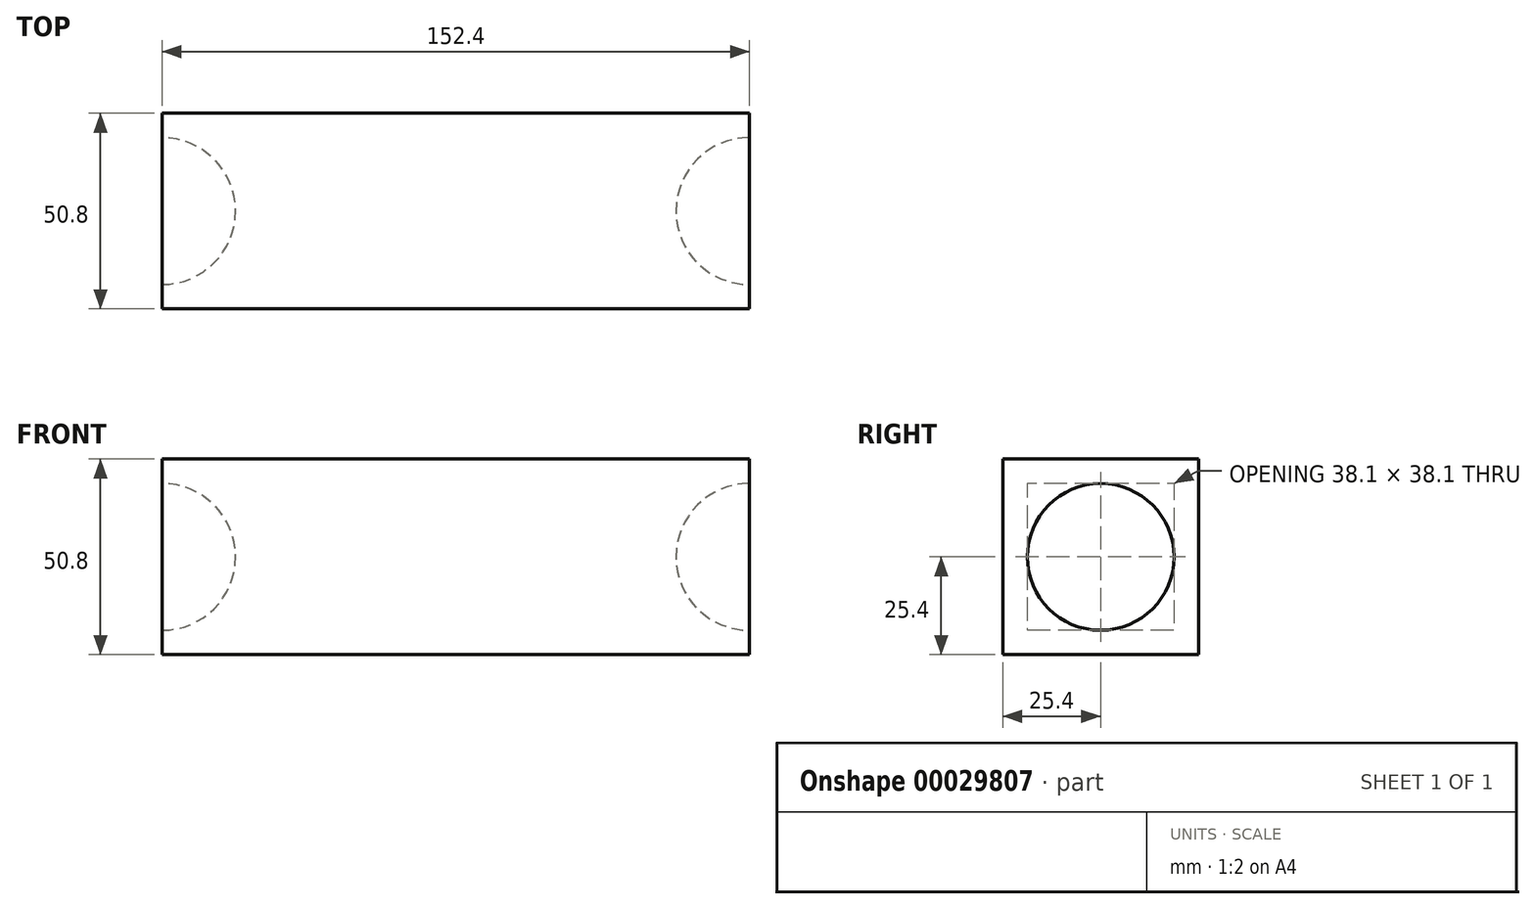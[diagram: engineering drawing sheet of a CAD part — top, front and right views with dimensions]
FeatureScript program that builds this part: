
annotation { "Feature Type Name" : "Feature", "Feature Type Description" : "" }
export const myFeature = defineFeature(function(context is Context, id is Id, definition is map)
    precondition{}
    {
        {
            var Q0;
            Q0=qCreatedBy(makeId("Front.planeOp"),FACE);
            var sketch = newSketch(context, id + "F0", { "sketchPlane" : qUnion([Q0])});
            skLineSegment(sketch, "E0.bottom", {"start": v(-73.68, 44.3) * mm, "end": v(78.72, 44.3) * mm});
            skLineSegment(sketch, "E0.top", {"start": v(-73.68, -6.5) * mm, "end": v(78.72, -6.5) * mm});
            skLineSegment(sketch, "E0.left", {"start": v(-73.68, 44.3) * mm, "end": v(-73.68, -6.5) * mm});
            skLineSegment(sketch, "E0.right", {"start": v(78.72, 44.3) * mm, "end": v(78.72, -6.5) * mm});
            skSolve(sketch);
        }
        {
            var Q0;
            Q0=makeQuery(id+"F0.imprint","IMPRINT",FACE,{"disambiguationData":[TD([[makeQuery(id+"F0.imprint","IMPRINT",EDGE,{"derivedFrom":sQuery(id+"F0.wireOp",EDGE,"E0.bottom")}),-1.0]])]});
            extrude(context, id + "F1", {"entities" : qUnion([Q0]), "depth" : 50.8 * mm});
        }
        {
            var Q0;
            Q0=makeQuery(id+"F1.opExtrude","SWEPT_FACE",FACE,{"disambiguationData":[OSD([sQuery(id+"F0.wireOp",EDGE,"E0.left")])]});
            var sketch = newSketch(context, id + "F2", { "sketchPlane" : qUnion([Q0])});
            skLineSegment(sketch, "E1", {"start": v(0, 18.9) * mm, "end": v(50.8, 18.9) * mm});
            skLineSegment(sketch, "E2", {"start": v(25.4, 44.3) * mm, "end": v(25.4, -6.5) * mm});
            skCircle(sketch, "E3", {"center": v(25.4, 18.9) * mm, "radius": 19.05 * mm});
            skSolve(sketch);
        }
        {
            var Q0;
            {var subQ0=sQuery(id+"F2.wireOp",EDGE,"E3");var subQ3=sQuery(id+"F2.wireOp",EDGE,"E1");var subQ4=makeQuery(id+"F2.imprint","INTERSECT",VERTEX,{"disambiguationData":[OD(0.0)],"derivedFrom":[subQ3,subQ0]});Q0=makeQuery(id+"F2.imprint","IMPRINT",FACE,{"disambiguationData":[TD([[makeQuery(id+"F2.imprint","IMPRINT",EDGE,{"disambiguationData":[TD([[subQ4,-1.0]])],"derivedFrom":subQ3}),-1.0]])]});}
            var Q1;
            {var subQ0=sQuery(id+"F2.wireOp",EDGE,"E3");var subQ3=sQuery(id+"F2.wireOp",EDGE,"E1");var subQ4=makeQuery(id+"F2.imprint","INTERSECT",VERTEX,{"disambiguationData":[OD(0.0)],"derivedFrom":[subQ3,subQ0]});Q1=makeQuery(id+"F2.imprint","IMPRINT",FACE,{"disambiguationData":[TD([[makeQuery(id+"F2.imprint","IMPRINT",EDGE,{"disambiguationData":[TD([[subQ4,-1.0]])],"derivedFrom":subQ3}),1.0]])]});}
            var Q2;
            Q2=sQuery(id+"F2.wireOp",EDGE,"E2");
            revolve(context, id + "F3", {"operationType" : NewBodyOperationType.REMOVE, "entities" : qUnion([Q0, Q1]), "axis" : qUnion([Q2]), "revolveType" : RevolveType.FULL, "oppositeDirection" : true});
        }
        {
            var Q0;
            Q0=makeQuery(id+"F1.opExtrude","SWEPT_FACE",FACE,{"disambiguationData":[OSD([sQuery(id+"F0.wireOp",EDGE,"E0.right")])]});
            var sketch = newSketch(context, id + "F4", { "sketchPlane" : qUnion([Q0])});
            skLineSegment(sketch, "E4", {"start": v(-50.8, 18.9) * mm, "end": v(0, 18.9) * mm});
            skLineSegment(sketch, "E5", {"start": v(-25.4, 44.3) * mm, "end": v(-25.4, -6.5) * mm});
            skCircle(sketch, "E6", {"center": v(-25.4, 18.9) * mm, "radius": 19.05 * mm});
            skSolve(sketch);
        }
        {
            var Q0;
            {var subQ0=sQuery(id+"F4.wireOp",EDGE,"E6");var subQ3=sQuery(id+"F4.wireOp",EDGE,"E4");var subQ4=makeQuery(id+"F4.imprint","INTERSECT",VERTEX,{"disambiguationData":[OD(0.0)],"derivedFrom":[subQ3,subQ0]});Q0=makeQuery(id+"F4.imprint","IMPRINT",FACE,{"disambiguationData":[TD([[makeQuery(id+"F4.imprint","IMPRINT",EDGE,{"disambiguationData":[TD([[subQ4,-1.0]])],"derivedFrom":subQ3}),1.0]])]});}
            var Q1;
            {var subQ0=sQuery(id+"F4.wireOp",EDGE,"E6");var subQ3=sQuery(id+"F4.wireOp",EDGE,"E4");var subQ4=makeQuery(id+"F4.imprint","INTERSECT",VERTEX,{"disambiguationData":[OD(0.0)],"derivedFrom":[subQ3,subQ0]});Q1=makeQuery(id+"F4.imprint","IMPRINT",FACE,{"disambiguationData":[TD([[makeQuery(id+"F4.imprint","IMPRINT",EDGE,{"disambiguationData":[TD([[subQ4,-1.0]])],"derivedFrom":subQ3}),-1.0]])]});}
            var Q2;
            Q2=sQuery(id+"F4.wireOp",EDGE,"E5");
            revolve(context, id + "F5", {"operationType" : NewBodyOperationType.REMOVE, "entities" : qUnion([Q0, Q1]), "axis" : qUnion([Q2]), "revolveType" : RevolveType.FULL, "oppositeDirection" : true});
        }
    });
